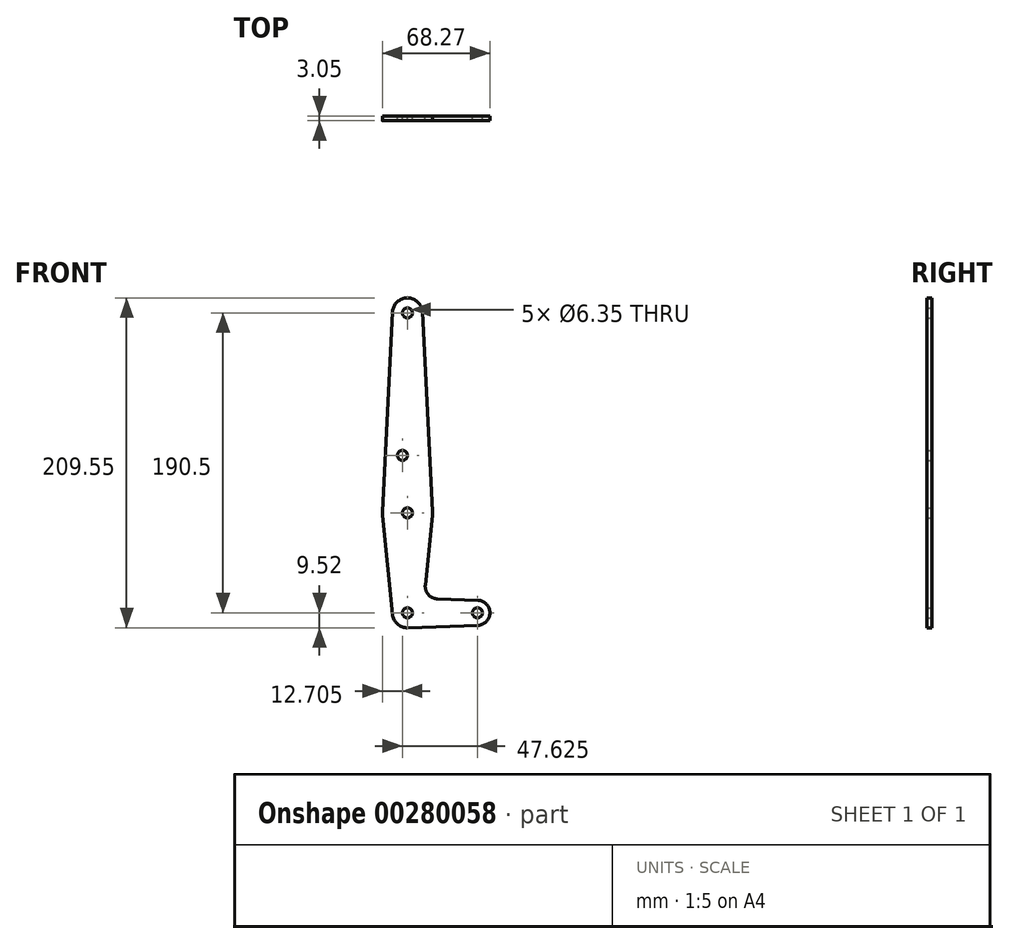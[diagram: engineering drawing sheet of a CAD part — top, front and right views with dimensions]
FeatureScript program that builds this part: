
annotation { "Feature Type Name" : "Feature", "Feature Type Description" : "" }
export const myFeature = defineFeature(function(context is Context, id is Id, definition is map)
    precondition{}
    {
        {
            var Q0;
            Q0=qCreatedBy(makeId("Front.planeOp"),FACE);
            var sketch = newSketch(context, id + "F0", { "sketchPlane" : qUnion([Q0])});
            skCircle(sketch, "E0", {"center": v(0, 63.5) * mm, "radius": 15.88 * mm});
            skCircle(sketch, "E1", {"center": v(0, 0) * mm, "radius": 9.53 * mm});
            skCircle(sketch, "E2", {"center": v(0, 190.5) * mm, "radius": 9.53 * mm});
            skCircle(sketch, "E3", {"center": v(44.45, 0) * mm, "radius": 7.94 * mm});
            skLineSegment(sketch, "E4", {"start": v(0, 0) * mm, "end": v(0, 190.5) * mm, "construction": true});
            skLineSegment(sketch, "E5", {"start": v(0, 0) * mm, "end": v(44.45, 0) * mm, "construction": true});
            skLineSegment(sketch, "E6", {"start": v(-9.51, 190.98) * mm, "end": v(-15.86, 64.3) * mm});
            skLineSegment(sketch, "E7", {"start": v(9.51, 190.98) * mm, "end": v(15.86, 64.3) * mm});
            skCircle(sketch, "E8", {"center": v(0, 190.5) * mm, "radius": 3.18 * mm});
            skCircle(sketch, "E9", {"center": v(0, 63.5) * mm, "radius": 3.18 * mm});
            skCircle(sketch, "E10", {"center": v(0, 0) * mm, "radius": 3.18 * mm});
            skCircle(sketch, "E11", {"center": v(44.45, 0) * mm, "radius": 3.18 * mm});
            skCircle(sketch, "E12", {"center": v(-3.18, 100.03) * mm, "radius": 3.18 * mm});
            skLineSegment(sketch, "E13", {"start": v(15.8, 61.91) * mm, "end": v(11.34, 17.6) * mm});
            skLineSegment(sketch, "E14", {"start": v(18.97, 8.85) * mm, "end": v(44.73, 7.93) * mm});
            skArc(sketch, "E15.filletArc", {"start": v(11.34, 17.6) * mm, "mid": v(13.26, 11.57) * mm, "end": v(18.97, 8.85) * mm});
            skLineSegment(sketch, "E16", {"start": v(-15.8, 61.91) * mm, "end": v(-9.48, -0.95) * mm});
            skLineSegment(sketch, "E17", {"start": v(0.34, -9.52) * mm, "end": v(44.73, -7.93) * mm});
            skSolve(sketch);
        }
        {
            var Q0;
            Q0 = qSketchRegion(id + "F0", true);
            extrude(context, id + "F1", {"entities" : qUnion([Q0]), "depth" : 3.05 * mm});
        }
    });
